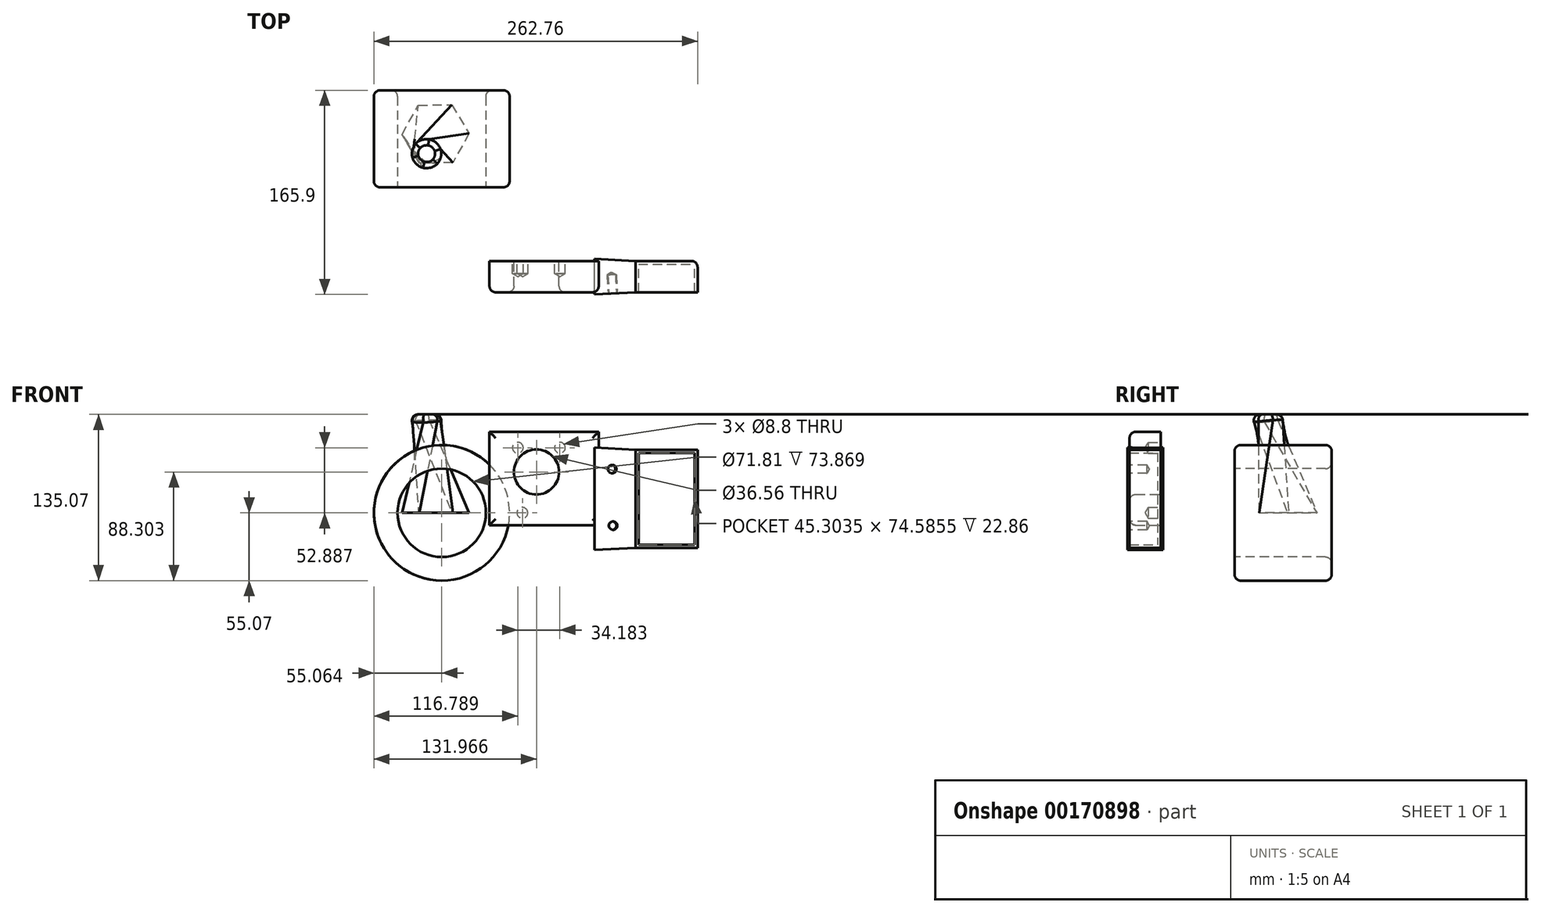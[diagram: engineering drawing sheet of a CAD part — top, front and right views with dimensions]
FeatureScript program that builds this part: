
annotation { "Feature Type Name" : "Feature", "Feature Type Description" : "" }
export const myFeature = defineFeature(function(context is Context, id is Id, definition is map)
    precondition{}
    {
        {
            var Q0;
            Q0=qCreatedBy(makeId("Front.planeOp"),FACE);
            var sketch = newSketch(context, id + "F0", { "sketchPlane" : qUnion([Q0])});
            skCircle(sketch, "E0", {"center": v(-43.75, 33.23) * mm, "radius": 18.28 * mm});
            skLineSegment(sketch, "E1.bottom", {"start": v(-81.91, 65.86) * mm, "end": v(6.76, 65.86) * mm});
            skLineSegment(sketch, "E1.top", {"start": v(-81.91, -10.02) * mm, "end": v(6.76, -10.02) * mm});
            skLineSegment(sketch, "E1.left", {"start": v(-81.91, 65.86) * mm, "end": v(-81.91, -10.02) * mm});
            skLineSegment(sketch, "E1.right", {"start": v(6.76, 65.86) * mm, "end": v(6.76, -10.02) * mm});
            skLineSegment(sketch, "E2.bottom", {"start": v(36.65, 51.32) * mm, "end": v(87.04, 51.32) * mm});
            skLineSegment(sketch, "E2.top", {"start": v(36.65, -28.35) * mm, "end": v(87.04, -28.35) * mm});
            skLineSegment(sketch, "E2.left", {"start": v(36.65, 51.32) * mm, "end": v(36.65, -28.35) * mm});
            skLineSegment(sketch, "E2.right", {"start": v(87.04, 51.32) * mm, "end": v(87.04, -28.35) * mm});
            skSolve(sketch);
        }
        {
            var Q0;
            Q0=makeQuery(id+"F0.imprint","IMPRINT",FACE,{"disambiguationData":[TD([[makeQuery(id+"F0.imprint","IMPRINT",EDGE,{"derivedFrom":sQuery(id+"F0.wireOp",EDGE,"E0")}),-1.0]])]});
            var Q1;
            Q1=makeQuery(id+"F0.imprint","IMPRINT",FACE,{"disambiguationData":[TD([[makeQuery(id+"F0.imprint","IMPRINT",EDGE,{"derivedFrom":sQuery(id+"F0.wireOp",EDGE,"E2.bottom")}),-1.0]])]});
            extrude(context, id + "F1", {"entities" : qUnion([Q0, Q1]), "depth" : 25.4 * mm});
        }
        {
            var Q0;
            Q0=makeQuery(id+"F1.opExtrude","CAP_FACE",FACE,{"disambiguationData":[OSD([sQuery(id+"F0.wireOp",EDGE,"E0"),sQuery(id+"F0.wireOp",EDGE,"E1.bottom"),sQuery(id+"F0.wireOp",EDGE,"E1.top"),sQuery(id+"F0.wireOp",EDGE,"E1.left"),sQuery(id+"F0.wireOp",EDGE,"E1.right")])],"isStart":false});
            fillet(context, id + "F2", {"entities" : qUnion([Q0]), "radius" : 5.08 * mm, "tangentPropagation" : true, "allowEdgeOverflow" : false});
        }
        {
            var Q0;
            Q0=makeQuery(id+"F1.opExtrude","CAP_FACE",FACE,{"disambiguationData":[OSD([sQuery(id+"F0.wireOp",EDGE,"E2.bottom"),sQuery(id+"F0.wireOp",EDGE,"E2.top"),sQuery(id+"F0.wireOp",EDGE,"E2.left"),sQuery(id+"F0.wireOp",EDGE,"E2.right")])],"isStart":false});
            shell(context, id + "F3", {"entities" : qUnion([Q0]), "thickness" : 2.54 * mm});
        }
        {
            var Q0;
            Q0=makeQuery(id+"F1.opExtrude","SWEPT_FACE",FACE,{"disambiguationData":[OSD([sQuery(id+"F0.wireOp",EDGE,"E2.left")])]});
            extrude(context, id + "F4", {"entities" : qUnion([Q0]), "operationType" : NewBodyOperationType.ADD, "depth" : 33.27 * mm, "hasDraft" : true, "draftAngle" : 3 * degree});
        }
        {
            var Q0;
            Q0=qCreatedBy(makeId("Top.planeOp"),FACE);
            var sketch = newSketch(context, id + "F5", { "sketchPlane" : qUnion([Q0])});
            skLineSegment(sketch, "E3", {"start": v(-120.66, 40.08) * mm, "end": v(-120.66, 134.16) * mm, "construction": true});
            skLineSegment(sketch, "E4.bottom", {"start": v(-84.75, 59.9) * mm, "end": v(-70.6, 59.9) * mm});
            skLineSegment(sketch, "E4.top", {"start": v(-84.75, 138.76) * mm, "end": v(-65.6, 138.76) * mm});
            skLineSegment(sketch, "E4.left", {"start": v(-84.75, 59.9) * mm, "end": v(-84.75, 138.76) * mm});
            skLineSegment(sketch, "E4.right", {"start": v(-65.6, 64.9) * mm, "end": v(-65.6, 138.76) * mm});
            skPoint(sketch, "E5.visualSharp", {"position": v(-65.6, 59.9) * mm});
            skArc(sketch, "E5.filletArc", {"start": v(-70.6, 59.9) * mm, "mid": v(-67.05, 61.36) * mm, "end": v(-65.6, 64.9) * mm});
            skSolve(sketch);
        }
        {
            var Q0;
            Q0=makeQuery(id+"F5.imprint","IMPRINT",FACE,{"disambiguationData":[TD([[makeQuery(id+"F5.imprint","IMPRINT",EDGE,{"derivedFrom":sQuery(id+"F5.wireOp",EDGE,"E4.bottom")}),1.0]])]});
            var Q1;
            Q1=sQuery(id+"F5.wireOp",EDGE,"E3");
            revolve(context, id + "F6", {"entities" : qUnion([Q0]), "axis" : qUnion([Q1]), "revolveType" : RevolveType.FULL});
        }
        {
            var Q0;
            Q0=qCreatedBy(makeId("Top.planeOp"),FACE);
            var sketch = newSketch(context, id + "F7", { "sketchPlane" : qUnion([Q0])});
            skCircle(sketch, "E6.cCircle", {"center": v(-125.7, 103.27) * mm, "radius": 23.55 * mm, "construction": true});
            skLineSegment(sketch, "E6.0", {"start": v(-98.5, 103.71) * mm, "end": v(-111.71, 79.95) * mm});
            skLineSegment(sketch, "E6.1", {"start": v(-111.71, 79.95) * mm, "end": v(-138.9, 79.5) * mm});
            skLineSegment(sketch, "E6.2", {"start": v(-138.9, 79.5) * mm, "end": v(-152.88, 102.82) * mm});
            skLineSegment(sketch, "E6.3", {"start": v(-152.88, 102.82) * mm, "end": v(-139.67, 126.58) * mm});
            skLineSegment(sketch, "E6.4", {"start": v(-139.67, 126.58) * mm, "end": v(-112.49, 127.03) * mm});
            skLineSegment(sketch, "E6.5", {"start": v(-112.49, 127.03) * mm, "end": v(-98.5, 103.71) * mm});
            skPoint(sketch, "E6.0.midPoint", {"position": v(-105.1, 91.83) * mm});
            skSolve(sketch);
        }
        {
            var Q0;
            Q0=qCreatedBy(makeId("Top.planeOp"),FACE);
            cPlane(context, id + "F8", {"entities" : qUnion([Q0]), "cplaneType" : CPlaneType.OFFSET, "offset" : 80 * mm, "width" : 150 * mm, "height" : 150 * mm});
        }
        {
            var Q0;
            Q0=qCreatedBy(id+"F8.planeOp",FACE);
            var sketch = newSketch(context, id + "F9", { "sketchPlane" : qUnion([Q0])});
            skCircle(sketch, "E7", {"center": v(-133.5, 86.06) * mm, "radius": 12.54 * mm});
            skSolve(sketch);
        }
        {
            var Q1;
            Q1=makeQuery(id+"F9.imprint","IMPRINT",FACE,{"disambiguationData":[TD([[makeQuery(id+"F9.imprint","IMPRINT",EDGE,{"derivedFrom":sQuery(id+"F9.wireOp",EDGE,"E7")}),1.0]])]});
            var Q2;
            Q2=makeQuery(id+"F7.imprint","IMPRINT",FACE,{"disambiguationData":[TD([[makeQuery(id+"F7.imprint","IMPRINT",EDGE,{"derivedFrom":sQuery(id+"F7.wireOp",EDGE,"E6.0")}),-1.0]])]});
            loft(context, id + "F10", {"sheetProfilesArray" : [{ "sheetProfileEntities" : qUnion([Q1]) }, { "sheetProfileEntities" : qUnion([Q2]) }]});
        }
        {
            var Q0;
            Q0=makeQuery(id+"F1.opExtrude","CAP_FACE",FACE,{"disambiguationData":[OSD([sQuery(id+"F0.wireOp",EDGE,"E0"),sQuery(id+"F0.wireOp",EDGE,"E1.bottom"),sQuery(id+"F0.wireOp",EDGE,"E1.top"),sQuery(id+"F0.wireOp",EDGE,"E1.left"),sQuery(id+"F0.wireOp",EDGE,"E1.right")])],"isStart":true});
            var sketch = newSketch(context, id + "F11", { "sketchPlane" : qUnion([Q0])});
            skPoint(sketch, "E8", {"position": v(24.75, 52.89) * mm});
            skPoint(sketch, "E9", {"position": v(58.93, 52.89) * mm});
            skPoint(sketch, "E10", {"position": v(55.15, 0) * mm});
            skSolve(sketch);
        }
        {
            var Q0;
            Q0=sQuery(id+"F11.wireOp",VERTEX,"E9");
            var Q1;
            Q1=sQuery(id+"F11.wireOp",VERTEX,"E8");
            var Q2;
            Q2=sQuery(id+"F11.wireOp",VERTEX,"E10");
            var Q3;
            Q3=makeQuery(id+"F1.opExtrude","SWEPT_BODY",BODY,{"disambiguationData":[OSD([sQuery(id+"F0.wireOp",EDGE,"E0"),sQuery(id+"F0.wireOp",EDGE,"E1.bottom"),sQuery(id+"F0.wireOp",EDGE,"E1.top"),sQuery(id+"F0.wireOp",EDGE,"E1.left"),sQuery(id+"F0.wireOp",EDGE,"E1.right")])]});
            hole(context, id + "F12", {"style" : HoleStyle.SIMPLE, "endStyle" : HoleEndStyle.BLIND, "standardTappedOrClearance" : lookupTablePath({ "standard" : "ISO", "fit" : "Normal", "size" : "M8", "type" : "Clearance" }), "standardBlindInLast" : lookupTablePath({ "fit" : "Standard", "standard" : "ISO", "size" : "M8", "type" : "Clearance" }), "holeDiameter" : 8.8 * mm, "holeDepth" : 10.1 * mm, "startFromSketch" : true, "locations" : qUnion([Q0, Q1, Q2]), "scope" : qUnion([Q3])});
        }
        {
            var Q0;
            Q0=makeQuery(id+"F1.opExtrude","CAP_EDGE",EDGE,{"disambiguationData":[OSD([sQuery(id+"F0.wireOp",EDGE,"E2.right")])],"isStart":true});
            var Q1;
            {var subQ0=sQuery(id+"F0.wireOp",EDGE,"E2.left");var subQ1=makeQuery(id+"F1.opExtrude","CAP_EDGE",EDGE,{"disambiguationData":[OSD([subQ0])],"isStart":true});Q1=makeQuery(id+"F4.boolean.opBoolean","MERGE",EDGE,{"derivedFrom":[subQ1,makeQuery(id+"F4.opExtrude","CAP_EDGE",EDGE,{"disambiguationData":[OSD([subQ0]),TDD([subQ1])],"isStart":true})]});}
            var Q2;
            Q2=makeQuery(id+"F6.opRevolve","SWEPT_EDGE",EDGE,{"disambiguationData":[OSD([sQuery(id+"F5.wireOp",EDGE,"E4.top"),sQuery(id+"F5.wireOp",EDGE,"E4.left")])]});
            var Q3;
            Q3=makeQuery(id+"F6.opRevolve","SWEPT_EDGE",EDGE,{"disambiguationData":[OSD([sQuery(id+"F5.wireOp",EDGE,"E4.top"),sQuery(id+"F5.wireOp",EDGE,"E4.right")])]});
            var Q4;
            Q4=makeQuery(id+"F10.opLoft","MID_CAP_EDGE",EDGE,{"disambiguationData":[OSD([sQuery(id+"F7.wireOp",EDGE,"E6.0"),sQuery(id+"F7.wireOp",EDGE,"E6.4"),sQuery(id+"F7.wireOp",EDGE,"E6.5"),sQuery(id+"F9.wireOp",EDGE,"E7")])],"capPos":0.0});
            var Q5;
            Q5=makeQuery(id+"F10.opLoft","MID_CAP_EDGE",EDGE,{"disambiguationData":[OSD([sQuery(id+"F7.wireOp",EDGE,"E6.3"),sQuery(id+"F7.wireOp",EDGE,"E6.4"),sQuery(id+"F7.wireOp",EDGE,"E6.5"),sQuery(id+"F9.wireOp",EDGE,"E7")])],"capPos":0.0});
            fillet(context, id + "F13", {"entities" : qUnion([Q0, Q1, Q2, Q3, Q4, Q5]), "radius" : 5 * mm, "tangentPropagation" : true, "allowEdgeOverflow" : false});
        }
        {
            var Q0;
            {var subQ0=sQuery(id+"F0.wireOp",EDGE,"E2.left");Q0=makeQuery(id+"F4.opExtrude","SWEPT_FACE",FACE,{"disambiguationData":[OSD([subQ0]),TDD([makeQuery(id+"F1.opExtrude","CAP_EDGE",EDGE,{"disambiguationData":[OSD([subQ0])],"isStart":false})])]});}
            var sketch = newSketch(context, id + "F14", { "sketchPlane" : qUnion([Q0])});
            skPoint(sketch, "E11", {"position": v(16.34, 35.56) * mm});
            skPoint(sketch, "E12", {"position": v(17.05, -10.41) * mm});
            skText(sketch, "E13", { "text": "B", "fontName": "OpenSans-Regular.ttf"});
            const initialGuessF14  = {"E13": [0.00842, -0.00032, 1, 0, 0.0294]};
            skSetInitialGuess(sketch, initialGuessF14);
            skSolve(sketch);
        }
        {
            var Q0;
            Q0=sQuery(id+"F14.wireOp",VERTEX,"E11");
            var Q1;
            Q1=sQuery(id+"F14.wireOp",VERTEX,"E12");
            var Q2;
            Q2=makeQuery(id+"F1.opExtrude","SWEPT_BODY",BODY,{"disambiguationData":[OSD([sQuery(id+"F0.wireOp",EDGE,"E0"),sQuery(id+"F0.wireOp",EDGE,"E1.bottom"),sQuery(id+"F0.wireOp",EDGE,"E1.top"),sQuery(id+"F0.wireOp",EDGE,"E1.left"),sQuery(id+"F0.wireOp",EDGE,"E1.right")])]});
            hole(context, id + "F15", {"style" : HoleStyle.SIMPLE, "endStyle" : HoleEndStyle.BLIND, "standardTappedOrClearance" : lookupTablePath({ "standard" : "ISO", "engagement" : "75%", "pitch" : "1.25 mm", "size" : "M8", "type" : "Tapped" }), "standardBlindInLast" : lookupTablePath({ "standard" : "ISO", "engagement" : "75%", "pitch" : "1.25 mm", "size" : "M8", "type" : "Tapped" }), "holeDiameter" : 6.8 * mm, "holeDepth" : 15.1 * mm, "startFromSketch" : true, "locations" : qUnion([Q0, Q1]), "scope" : qUnion([Q2]), "majorDiameter" : 8 * mm});
        }
    });
